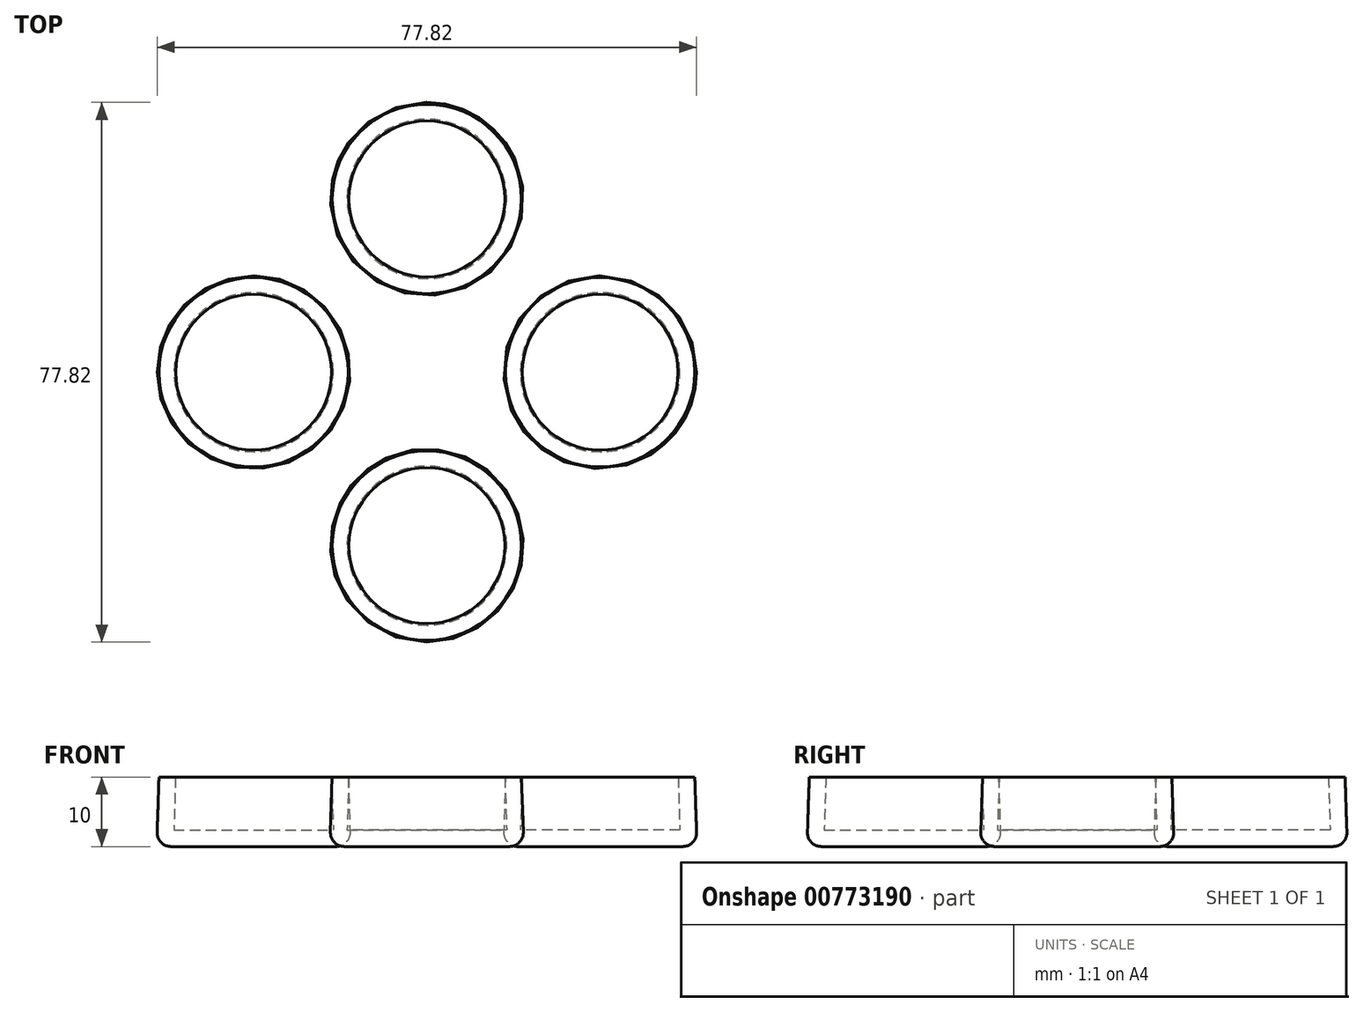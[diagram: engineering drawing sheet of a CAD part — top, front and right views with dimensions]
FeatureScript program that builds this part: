
annotation { "Feature Type Name" : "Feature", "Feature Type Description" : "" }
export const myFeature = defineFeature(function(context is Context, id is Id, definition is map)
    precondition{}
    {
        {
            var Q0;
            Q0=qCreatedBy(makeId("Front.planeOp"),FACE);
            var sketch = newSketch(context, id + "F0", { "sketchPlane" : qUnion([Q0])});
            skLineSegment(sketch, "E0", {"start": v(0, 0) * mm, "end": v(0, 14.01) * mm, "construction": true});
            skLineSegment(sketch, "E1", {"start": v(0, 0) * mm, "end": v(6.86, 0) * mm});
            skLineSegment(sketch, "E2", {"start": v(8.86, 2.13) * mm, "end": v(8, 14.97) * mm});
            skLineSegment(sketch, "E3", {"start": v(8, 14.97) * mm, "end": v(6, 14.97) * mm});
            skLineSegment(sketch, "E4", {"start": v(6, 14.97) * mm, "end": v(6, 2.4) * mm});
            skLineSegment(sketch, "E5", {"start": v(6, 2.4) * mm, "end": v(0, 2.4) * mm});
            skLineSegment(sketch, "E6", {"start": v(0, 2.4) * mm, "end": v(0, 0) * mm});
            skPoint(sketch, "E7.visualSharp", {"position": v(9, 0) * mm});
            skArc(sketch, "E7.filletArc", {"start": v(6.86, 0) * mm, "mid": v(8.32, 0.63) * mm, "end": v(8.86, 2.13) * mm});
            skSolve(sketch);
        }
        {
            var Q0;
            Q0=qCreatedBy(makeId("Front.planeOp"),FACE);
            var sketch = newSketch(context, id + "F1", { "sketchPlane" : qUnion([Q0])});
            skLineSegment(sketch, "E8", {"start": v(0, 0) * mm, "end": v(0, 37.18) * mm, "construction": true});
            skLineSegment(sketch, "E9", {"start": v(0, 0) * mm, "end": v(13.98, 0) * mm});
            skLineSegment(sketch, "E10", {"start": v(13.98, 0) * mm, "end": v(13.65, 10) * mm});
            skLineSegment(sketch, "E11", {"start": v(13.65, 10) * mm, "end": v(11.25, 10) * mm});
            skLineSegment(sketch, "E12", {"start": v(11.25, 10) * mm, "end": v(11.5, 2.4) * mm});
            skLineSegment(sketch, "E13", {"start": v(11.5, 2.4) * mm, "end": v(0, 2.4) * mm});
            skLineSegment(sketch, "E14", {"start": v(0, 2.4) * mm, "end": v(0, 0) * mm});
            skSolve(sketch);
        }
        {
            var Q0;
            Q0=makeQuery(id+"F1.imprint","IMPRINT",FACE,{"disambiguationData":[TD([[makeQuery(id+"F1.imprint","IMPRINT",EDGE,{"derivedFrom":sQuery(id+"F1.wireOp",EDGE,"E9")}),1.0]])]});
            var Q1;
            Q1=sQuery(id+"F1.wireOp",EDGE,"E8");
            revolve(context, id + "F2", {"surfaceOperationType" : NewSurfaceOperationType.NEW, "entities" : qUnion([Q0]), "axis" : qUnion([Q1]), "revolveType" : RevolveType.FULL});
        }
        {
            var Q0;
            Q0=makeQuery(id+"F2.opRevolve","SWEPT_EDGE",EDGE,{"disambiguationData":[OSD([sQuery(id+"F1.wireOp",EDGE,"E9"),sQuery(id+"F1.wireOp",EDGE,"E10")])]});
            fillet(context, id + "F3", {"entities" : qUnion([Q0]), "radius" : 2 * mm, "tangentPropagation" : true, "allowEdgeOverflow" : false});
        }
        {
            var Q0;
            Q0=qCreatedBy(makeId("Front.planeOp"),FACE);
            var sketch = newSketch(context, id + "F4", { "sketchPlane" : qUnion([Q0])});
            skLineSegment(sketch, "E15", {"start": v(25, 0) * mm, "end": v(25, 17.9) * mm, "construction": true});
            skSolve(sketch);
        }
        {
            var Q0;
            Q0=makeQuery(id+"F2.opRevolve","SWEPT_BODY",BODY,{"disambiguationData":[OSD([sQuery(id+"F1.wireOp",EDGE,"E9"),sQuery(id+"F1.wireOp",EDGE,"E10"),sQuery(id+"F1.wireOp",EDGE,"E11"),sQuery(id+"F1.wireOp",EDGE,"E12"),sQuery(id+"F1.wireOp",EDGE,"E13"),sQuery(id+"F1.wireOp",EDGE,"E14")])]});
            var Q1;
            Q1=sQuery(id+"F4.wireOp",EDGE,"E15");
            circularPattern(context, id + "F5", {"entities" : qUnion([Q0]), "axis" : qUnion([Q1]), "angle" : 360 * degree, "instanceCount" : 4, "equalSpace" : true});
        }
    });
